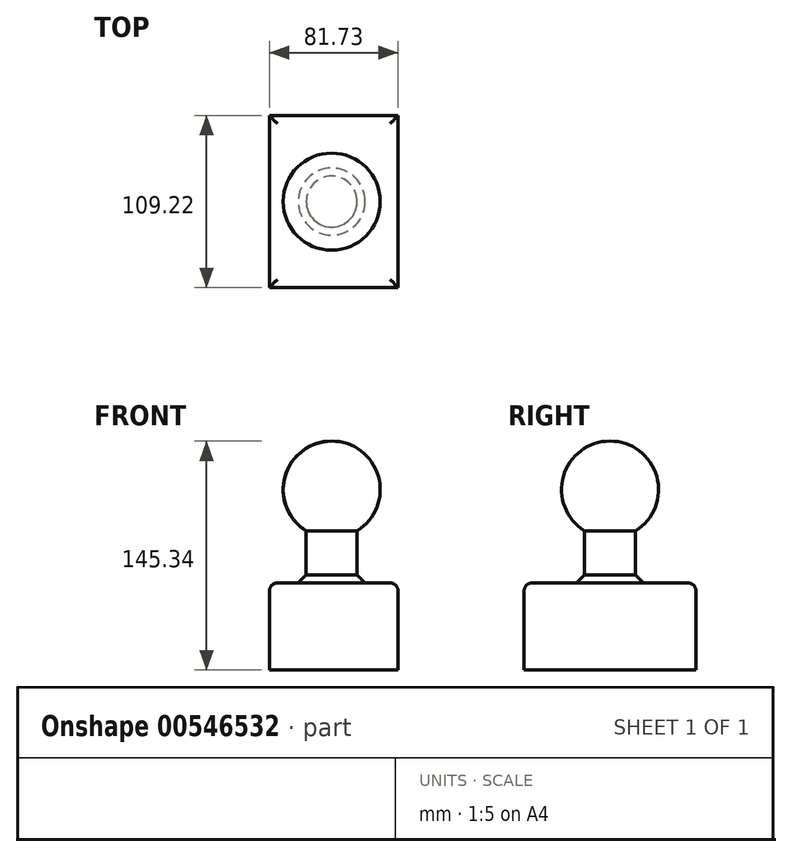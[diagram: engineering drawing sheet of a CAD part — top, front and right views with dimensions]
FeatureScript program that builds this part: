
annotation { "Feature Type Name" : "Feature", "Feature Type Description" : "" }
export const myFeature = defineFeature(function(context is Context, id is Id, definition is map)
    precondition{}
    {
        {
            var Q0;
            Q0=qCreatedBy(makeId("Front.planeOp"),FACE);
            var sketch = newSketch(context, id + "F0", { "sketchPlane" : qUnion([Q0])});
            skLineSegment(sketch, "E0.bottom", {"start": v(-39.54, 28.52) * mm, "end": v(42.2, 28.52) * mm});
            skLineSegment(sketch, "E0.top", {"start": v(-39.54, -26.67) * mm, "end": v(42.2, -26.67) * mm});
            skLineSegment(sketch, "E0.left", {"start": v(-39.54, 28.52) * mm, "end": v(-39.54, -26.67) * mm});
            skLineSegment(sketch, "E0.right", {"start": v(42.2, 28.52) * mm, "end": v(42.2, -26.67) * mm});
            skSolve(sketch);
        }
        {
            var Q0;
            Q0=makeQuery(id+"F0.imprint","IMPRINT",FACE,{"disambiguationData":[TD([[makeQuery(id+"F0.imprint","IMPRINT",EDGE,{"derivedFrom":sQuery(id+"F0.wireOp",EDGE,"E0.bottom")}),-1.0]])]});
            extrude(context, id + "F1", {"entities" : qUnion([Q0]), "endBound" : BoundingType.SYMMETRIC, "depth" : 109.22 * mm, "offsetDistance" : 25.4 * mm});
        }
        {
            var Q0;
            Q0=qCreatedBy(makeId("Front.planeOp"),FACE);
            var sketch = newSketch(context, id + "F2", { "sketchPlane" : qUnion([Q0])});
            skLineSegment(sketch, "E1", {"start": v(0, 69.66) * mm, "end": v(0, 13.4) * mm});
            skLineSegment(sketch, "E2", {"start": v(0, 13.4) * mm, "end": v(-16.19, 13.4) * mm});
            skLineSegment(sketch, "E3", {"start": v(-16.19, 13.4) * mm, "end": v(-16.19, 69.66) * mm});
            skLineSegment(sketch, "E4", {"start": v(-16.19, 69.66) * mm, "end": v(0, 69.66) * mm});
            skSolve(sketch);
        }
        {
            var Q0;
            Q0=makeQuery(id+"F2.imprint","IMPRINT",FACE,{"disambiguationData":[TD([[makeQuery(id+"F2.imprint","IMPRINT",EDGE,{"derivedFrom":sQuery(id+"F2.wireOp",EDGE,"E1")}),-1.0]])]});
            var Q1;
            Q1=sQuery(id+"F2.wireOp",EDGE,"E1");
            revolve(context, id + "F3", {"operationType" : NewBodyOperationType.ADD, "entities" : qUnion([Q0]), "axis" : qUnion([Q1]), "revolveType" : RevolveType.FULL});
        }
        {
            var Q0;
            Q0=qCreatedBy(makeId("Front.planeOp"),FACE);
            var sketch = newSketch(context, id + "F4", { "sketchPlane" : qUnion([Q0])});
            skArc(sketch, "E5", {"start": v(0, 118.67) * mm, "mid": v(-30.82, 87.85) * mm, "end": v(0, 57.03) * mm});
            skLineSegment(sketch, "E6", {"start": v(0, 118.67) * mm, "end": v(0, 57.03) * mm});
            skSolve(sketch);
        }
        {
            var Q0;
            Q0=makeQuery(id+"F4.imprint","IMPRINT",FACE,{"disambiguationData":[TD([[makeQuery(id+"F4.imprint","IMPRINT",EDGE,{"derivedFrom":sQuery(id+"F4.wireOp",EDGE,"E5")}),1.0]])]});
            var Q1;
            Q1=sQuery(id+"F4.wireOp",EDGE,"E6");
            revolve(context, id + "F5", {"operationType" : NewBodyOperationType.ADD, "entities" : qUnion([Q0]), "axis" : qUnion([Q1]), "revolveType" : RevolveType.FULL});
        }
        {
            var Q0;
            Q0=makeQuery(id+"F1.opExtrude","CAP_EDGE",EDGE,{"disambiguationData":[OSD([sQuery(id+"F0.wireOp",EDGE,"E0.bottom")])],"isStart":false});
            var Q1;
            Q1=makeQuery(id+"F1.opExtrude","SWEPT_EDGE",EDGE,{"disambiguationData":[OSD([sQuery(id+"F0.wireOp",EDGE,"E0.bottom"),sQuery(id+"F0.wireOp",EDGE,"E0.right")])]});
            var Q2;
            Q2=makeQuery(id+"F1.opExtrude","CAP_EDGE",EDGE,{"disambiguationData":[OSD([sQuery(id+"F0.wireOp",EDGE,"E0.bottom")])],"isStart":true});
            var Q3;
            Q3=makeQuery(id+"F1.opExtrude","SWEPT_EDGE",EDGE,{"disambiguationData":[OSD([sQuery(id+"F0.wireOp",EDGE,"E0.bottom"),sQuery(id+"F0.wireOp",EDGE,"E0.left")])]});
            fillet(context, id + "F6", {"entities" : qUnion([Q0, Q1, Q2, Q3]), "radius" : 5.08 * mm, "tangentPropagation" : true, "allowEdgeOverflow" : false});
        }
        {
            var Q0;
            Q0=makeQuery(id+"F3.boolean.opBoolean","INTERSECT",EDGE,{"derivedFrom":[makeQuery(id+"F1.opExtrude","SWEPT_FACE",FACE,{"disambiguationData":[OSD([sQuery(id+"F0.wireOp",EDGE,"E0.bottom")])]}),makeQuery(id+"F3.opRevolve","SWEPT_FACE",FACE,{"disambiguationData":[OSD([sQuery(id+"F2.wireOp",EDGE,"E3")])]})]});
            chamfer(context, id + "F7", {"entities" : qUnion([Q0]), "width" : 5.08 * mm, "tangentPropagation" : true});
        }
    });
